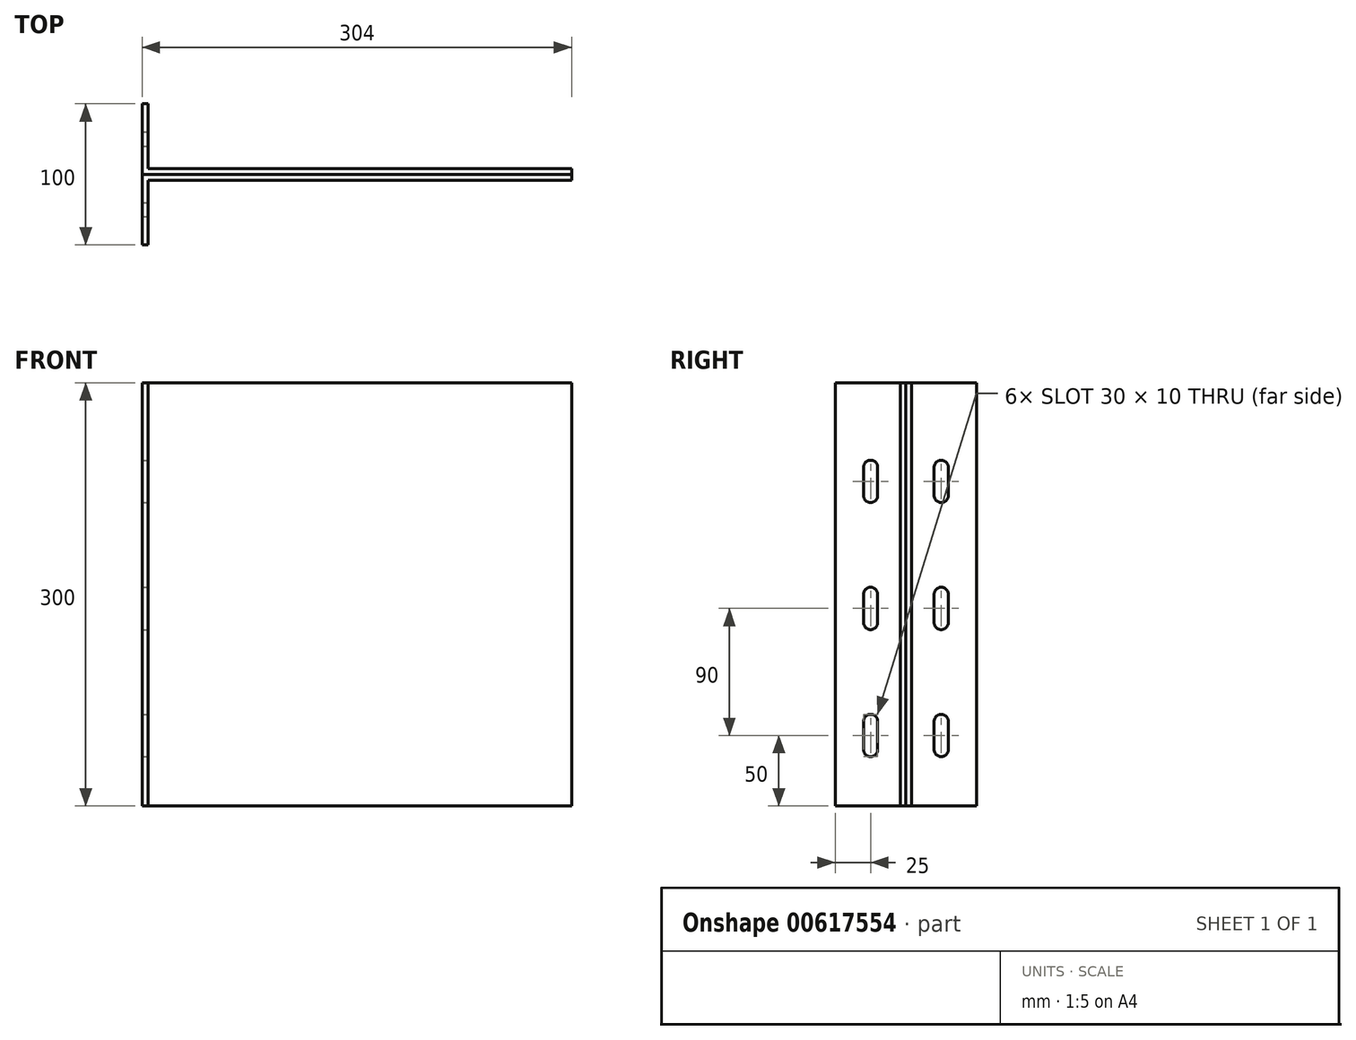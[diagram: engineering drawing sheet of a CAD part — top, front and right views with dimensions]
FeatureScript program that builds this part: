
annotation { "Feature Type Name" : "Feature", "Feature Type Description" : "" }
export const myFeature = defineFeature(function(context is Context, id is Id, definition is map)
    precondition{}
    {
        {
            var Q0;
            Q0=qCreatedBy(makeId("Front.planeOp"),FACE);
            var sketch = newSketch(context, id + "F0", { "sketchPlane" : qUnion([Q0])});
            skLineSegment(sketch, "E0.bottom", {"start": v(0, 0) * mm, "end": v(300, 0) * mm});
            skLineSegment(sketch, "E0.top", {"start": v(0, -300) * mm, "end": v(300, -300) * mm});
            skLineSegment(sketch, "E0.left", {"start": v(0, 0) * mm, "end": v(0, -300) * mm});
            skLineSegment(sketch, "E0.right", {"start": v(300, 0) * mm, "end": v(300, -300) * mm});
            skSolve(sketch);
        }
        {
            var Q0;
            Q0 = qSketchRegion(id + "F0", true);
            extrude(context, id + "F1", {"entities" : qUnion([Q0]), "depth" : 4 * mm, "offsetDistance" : 25 * mm});
        }
        {
            var Q0;
            Q0=qCreatedBy(makeId("Right.planeOp"),FACE);
            var sketch = newSketch(context, id + "F2", { "sketchPlane" : qUnion([Q0])});
            skLineSegment(sketch, "E1.bottom", {"start": v(0, 0) * mm, "end": v(-50, 0) * mm});
            skLineSegment(sketch, "E1.top", {"start": v(0, -300) * mm, "end": v(-50, -300) * mm});
            skLineSegment(sketch, "E1.left", {"start": v(0, 0) * mm, "end": v(0, -300) * mm});
            skLineSegment(sketch, "E1.right", {"start": v(-50, 0) * mm, "end": v(-50, -300) * mm});
            skSolve(sketch);
        }
        {
            var Q0;
            Q0 = qSketchRegion(id + "F2", true);
            extrude(context, id + "F3", {"entities" : qUnion([Q0]), "operationType" : NewBodyOperationType.ADD, "oppositeDirection" : true, "depth" : 4 * mm, "offsetDistance" : 25 * mm});
        }
        {
            var Q0;
            Q0=makeQuery(id+"F3.opExtrude","CAP_FACE",FACE,{"disambiguationData":[OSD([sQuery(id+"F2.wireOp",EDGE,"E1.bottom"),sQuery(id+"F2.wireOp",EDGE,"E1.top"),sQuery(id+"F2.wireOp",EDGE,"E1.left"),sQuery(id+"F2.wireOp",EDGE,"E1.right")])],"isStart":true});
            var sketch = newSketch(context, id + "F4", { "sketchPlane" : qUnion([Q0])});
            skArc(sketch, "E2", {"start": v(-20, -60) * mm, "mid": v(-25, -55) * mm, "end": v(-30, -60) * mm});
            skArc(sketch, "E3", {"start": v(-30, -80) * mm, "mid": v(-25, -85) * mm, "end": v(-20, -80) * mm});
            skLineSegment(sketch, "E4", {"start": v(-32.39, -63.38) * mm, "end": v(-31.95, -62.53) * mm});
            skLineSegment(sketch, "E5", {"start": v(-30, -60) * mm, "end": v(-30, -80) * mm});
            skLineSegment(sketch, "E6", {"start": v(-20, -60) * mm, "end": v(-20, -80) * mm});
            skArc(sketch, "E7", {"start": v(-20, -150) * mm, "mid": v(-25, -145) * mm, "end": v(-30, -150) * mm});
            skArc(sketch, "E8", {"start": v(-30, -170) * mm, "mid": v(-25, -175) * mm, "end": v(-20, -170) * mm});
            skLineSegment(sketch, "E9", {"start": v(-30, -150) * mm, "end": v(-30, -170) * mm});
            skLineSegment(sketch, "E10", {"start": v(-20, -150) * mm, "end": v(-20, -170) * mm});
            skArc(sketch, "E11", {"start": v(-20, -240) * mm, "mid": v(-25, -235) * mm, "end": v(-30, -240) * mm});
            skArc(sketch, "E12", {"start": v(-30, -260) * mm, "mid": v(-25, -265) * mm, "end": v(-20, -260) * mm});
            skLineSegment(sketch, "E13", {"start": v(-30, -240) * mm, "end": v(-30, -260) * mm});
            skLineSegment(sketch, "E14", {"start": v(-20, -240) * mm, "end": v(-20, -260) * mm});
            skSolve(sketch);
        }
        {
            var Q0;
            Q0 = qSketchRegion(id + "F4", true);
            extrude(context, id + "F5", {"entities" : qUnion([Q0]), "operationType" : NewBodyOperationType.REMOVE, "oppositeDirection" : true, "depth" : 25 * mm, "offsetDistance" : 25 * mm});
        }
        {
            var Q0;
            Q0=qCreatedBy(makeId("Front.planeOp"),FACE);
            var sketch = newSketch(context, id + "F6", { "sketchPlane" : qUnion([Q0])});
            skLineSegment(sketch, "E15.bottom", {"start": v(300, 0) * mm, "end": v(270, 0) * mm});
            skLineSegment(sketch, "E15.top", {"start": v(300, -40) * mm, "end": v(270, -40) * mm});
            skLineSegment(sketch, "E15.left", {"start": v(300, 0) * mm, "end": v(300, -40) * mm});
            skLineSegment(sketch, "E15.right", {"start": v(270, 0) * mm, "end": v(270, -40) * mm});
            skLineSegment(sketch, "E16.bottom", {"start": v(300, -260) * mm, "end": v(270, -260) * mm});
            skLineSegment(sketch, "E16.top", {"start": v(300, -300) * mm, "end": v(270, -300) * mm});
            skLineSegment(sketch, "E16.left", {"start": v(300, -260) * mm, "end": v(300, -300) * mm});
            skLineSegment(sketch, "E16.right", {"start": v(270, -260) * mm, "end": v(270, -300) * mm});
            skLineSegment(sketch, "E17.bottom", {"start": v(26, 0) * mm, "end": v(-4, 0) * mm});
            skLineSegment(sketch, "E17.top", {"start": v(26, -40) * mm, "end": v(-4, -40) * mm});
            skLineSegment(sketch, "E17.left", {"start": v(26, 0) * mm, "end": v(26, -40) * mm});
            skLineSegment(sketch, "E17.right", {"start": v(-4, 0) * mm, "end": v(-4, -40) * mm});
            skLineSegment(sketch, "E18.bottom", {"start": v(76, -260) * mm, "end": v(46, -260) * mm});
            skLineSegment(sketch, "E18.top", {"start": v(76, -300) * mm, "end": v(46, -300) * mm});
            skLineSegment(sketch, "E18.left", {"start": v(76, -260) * mm, "end": v(76, -300) * mm});
            skLineSegment(sketch, "E18.right", {"start": v(46, -260) * mm, "end": v(46, -300) * mm});
            skSolve(sketch);
        }
        {
            var Q0;
            Q0=makeQuery(id+"F6.imprint","IMPRINT",FACE,{"disambiguationData":[TD([[makeQuery(id+"F6.imprint","IMPRINT",EDGE,{"derivedFrom":sQuery(id+"F6.wireOp",EDGE,"E18.bottom")}),1.0]])]});
            var Q1;
            Q1=makeQuery(id+"F6.imprint","IMPRINT",FACE,{"disambiguationData":[TD([[makeQuery(id+"F6.imprint","IMPRINT",EDGE,{"derivedFrom":sQuery(id+"F6.wireOp",EDGE,"E16.bottom")}),1.0]])]});
            var Q2;
            Q2=sQuery(id+"F6.wireOp",EDGE,"E15.right");
            var Q3;
            Q3=sQuery(id+"F6.wireOp",EDGE,"E15.left");
            var Q4;
            Q4=sQuery(id+"F6.wireOp",EDGE,"E15.bottom");
            var Q5;
            Q5=sQuery(id+"F6.wireOp",EDGE,"E15.top");
            var Q6;
            Q6=sQuery(id+"F6.wireOp",EDGE,"E16.right");
            var Q7;
            Q7=sQuery(id+"F6.wireOp",EDGE,"E16.bottom");
            var Q8;
            Q8=sQuery(id+"F6.wireOp",EDGE,"E16.left");
            var Q9;
            Q9=sQuery(id+"F6.wireOp",EDGE,"E16.top");
            var Q10;
            Q10=sQuery(id+"F6.wireOp",EDGE,"E18.top");
            var Q11;
            Q11=sQuery(id+"F6.wireOp",EDGE,"E18.left");
            var Q12;
            Q12=sQuery(id+"F6.wireOp",EDGE,"E18.right");
            var Q13;
            Q13=sQuery(id+"F6.wireOp",EDGE,"E18.bottom");
            var Q14;
            Q14=sQuery(id+"F6.wireOp",EDGE,"E17.right");
            var Q15;
            Q15=sQuery(id+"F6.wireOp",EDGE,"E17.left");
            var Q16;
            Q16=sQuery(id+"F6.wireOp",EDGE,"E17.top");
            var Q17;
            Q17=sQuery(id+"F6.wireOp",EDGE,"E17.bottom");
            extrude(context, id + "F7", {"entities" : qUnion([Q0, Q1]), "bodyType" : ToolBodyType.SURFACE, "operationType" : NewBodyOperationType.ADD, "surfaceEntities" : qUnion([Q2, Q3, Q4, Q5, Q6, Q7, Q8, Q9, Q10, Q11, Q12, Q13, Q14, Q15, Q16, Q17]), "oppositeDirection" : true, "depth" : 2450 * mm, "offsetDistance" : 25 * mm});
        }
        {
            var Q0;
            Q0=makeQuery(id+"F1.opExtrude","SWEPT_BODY",BODY,{"disambiguationData":[OSD([sQuery(id+"F0.wireOp",EDGE,"E0.bottom"),sQuery(id+"F0.wireOp",EDGE,"E0.top"),sQuery(id+"F0.wireOp",EDGE,"E0.left"),sQuery(id+"F0.wireOp",EDGE,"E0.right")])]});
            var Q1;
            Q1=makeQuery(id+"F3.boolean.opBoolean","MERGE",FACE,{"derivedFrom":[makeQuery(id+"F1.opExtrude","CAP_FACE",FACE,{"disambiguationData":[OSD([sQuery(id+"F0.wireOp",EDGE,"E0.bottom"),sQuery(id+"F0.wireOp",EDGE,"E0.top"),sQuery(id+"F0.wireOp",EDGE,"E0.left"),sQuery(id+"F0.wireOp",EDGE,"E0.right")])],"isStart":true}),makeQuery(id+"F3.opExtrude","SWEPT_FACE",FACE,{"disambiguationData":[OSD([sQuery(id+"F2.wireOp",EDGE,"E1.left")])]})]});
            var Q2;
            Q2=makeQuery(id+"F3.opExtrude","CAP_FACE",FACE,{"disambiguationData":[OSD([sQuery(id+"F2.wireOp",EDGE,"E1.bottom"),sQuery(id+"F2.wireOp",EDGE,"E1.top"),sQuery(id+"F2.wireOp",EDGE,"E1.left"),sQuery(id+"F2.wireOp",EDGE,"E1.right")])],"isStart":false});
            var Q3;
            Q3=qCreatedBy(makeId("Front.planeOp"),FACE);
            mirror(context, id + "F8", {"entities" : qUnion([Q0]), "faces" : qUnion([Q1, Q2]), "mirrorPlane" : qUnion([Q3])});
        }
    });
